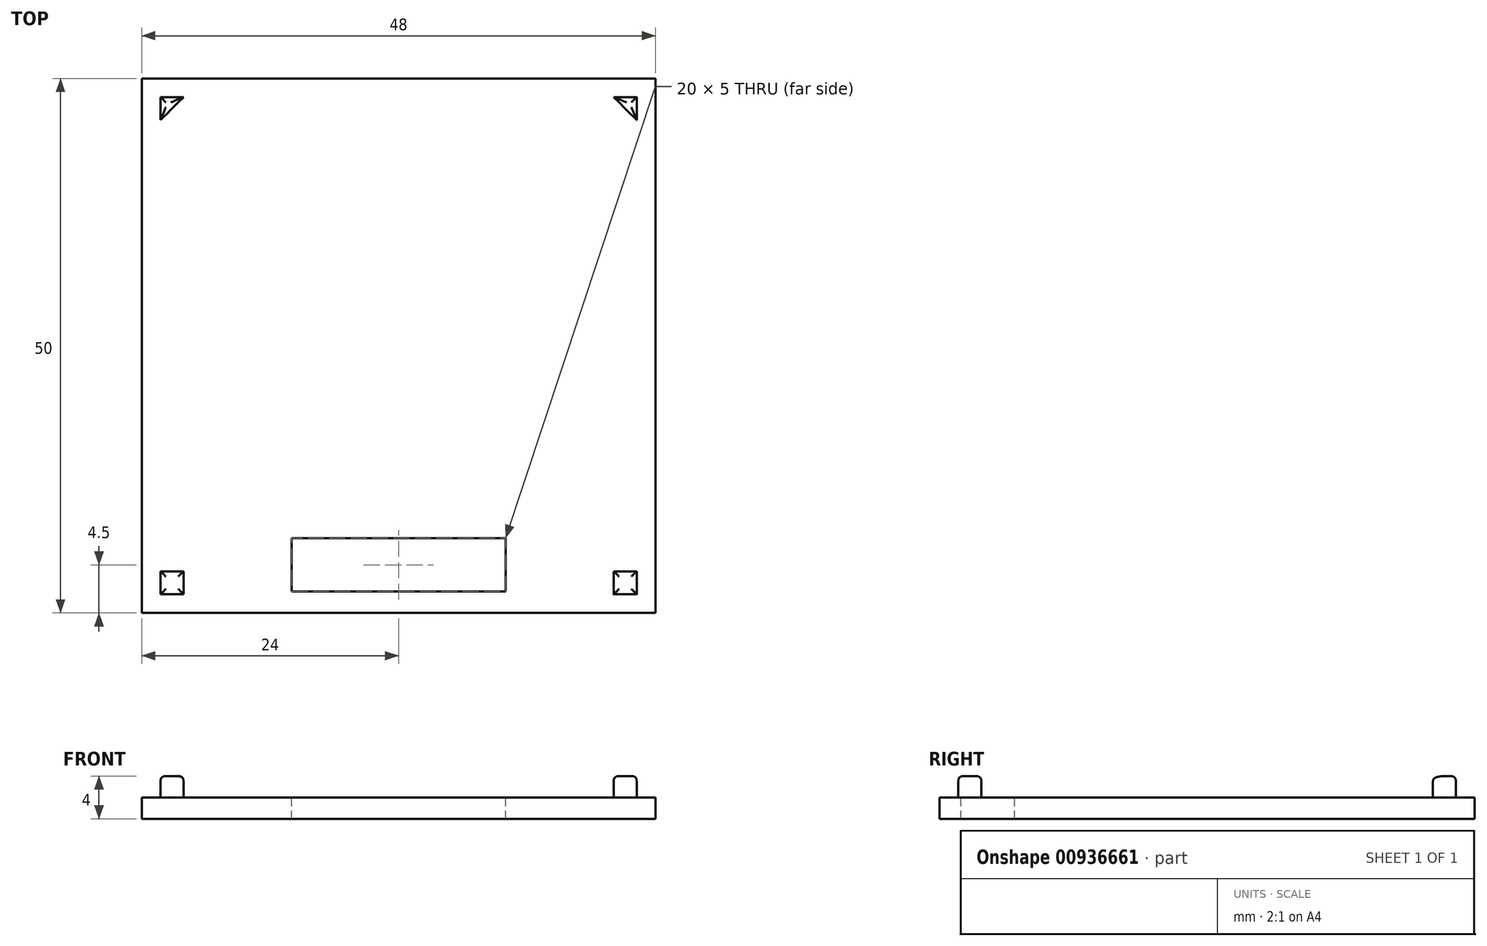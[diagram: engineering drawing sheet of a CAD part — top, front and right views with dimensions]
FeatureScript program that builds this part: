
annotation { "Feature Type Name" : "Feature", "Feature Type Description" : "" }
export const myFeature = defineFeature(function(context is Context, id is Id, definition is map)
    precondition{}
    {
        {
            var Q0;
            Q0=qCreatedBy(makeId("Top.planeOp"),FACE);
            var sketch = newSketch(context, id + "F0", { "sketchPlane" : qUnion([Q0])});
            skLineSegment(sketch, "E0.bottom", {"start": v(0, 0) * mm, "end": v(48, 0) * mm});
            skLineSegment(sketch, "E0.top", {"start": v(0, -50) * mm, "end": v(48, -50) * mm});
            skLineSegment(sketch, "E0.left", {"start": v(0, 0) * mm, "end": v(0, -50) * mm});
            skLineSegment(sketch, "E0.right", {"start": v(48, 0) * mm, "end": v(48, -50) * mm});
            skSolve(sketch);
        }
        {
            var Q0;
            Q0=makeQuery(id+"F0.imprint","IMPRINT",FACE,{"disambiguationData":[TD([[makeQuery(id+"F0.imprint","IMPRINT",EDGE,{"derivedFrom":sQuery(id+"F0.wireOp",EDGE,"8EBudFLo-aEb5-milo-hGKJ-UnPFVyJPno7u")}),1.0]])]});
            var Q1;
            Q1=makeQuery(id+"F0.imprint","IMPRINT",FACE,{"disambiguationData":[TD([[makeQuery(id+"F0.imprint","IMPRINT",EDGE,{"derivedFrom":sQuery(id+"F0.wireOp",EDGE,"b2cc03f5-71c5-4ed7-81ff-36fc711708750.MirrorCS")}),-1.0]])]});
            var Q2;
            Q2=makeQuery(id+"F0.imprint","IMPRINT",FACE,{"disambiguationData":[TD([[makeQuery(id+"F0.imprint","IMPRINT",EDGE,{"derivedFrom":sQuery(id+"F0.wireOp",EDGE,"E0.bottom")}),-1.0]])]});
            extrude(context, id + "F1", {"entities" : qUnion([Q0, Q1, Q2]), "depth" : 2 * mm, "offsetDistance" : 25 * mm});
        }
        {
            var Q0;
            Q0=makeQuery(id+"F1.opExtrude","CAP_FACE",FACE,{"disambiguationData":[OSD([sQuery(id+"F0.wireOp",EDGE,"E0.bottom"),sQuery(id+"F0.wireOp",EDGE,"E0.top"),sQuery(id+"F0.wireOp",EDGE,"E0.left"),sQuery(id+"F0.wireOp",EDGE,"E0.right")])],"isStart":false});
            var sketch = newSketch(context, id + "F2", { "sketchPlane" : qUnion([Q0])});
            skLineSegment(sketch, "E1", {"start": v(1.5, -1.5) * mm, "end": v(1.5, -4.5) * mm, "construction": true});
            skLineSegment(sketch, "E2", {"start": v(1.5, -4.5) * mm, "end": v(4.5, -1.5) * mm, "construction": true});
            skLineSegment(sketch, "E3", {"start": v(4.5, -1.5) * mm, "end": v(1.5, -1.5) * mm, "construction": true});
            skLineSegment(sketch, "E4.0", {"start": v(1.75, -3.9) * mm, "end": v(3.9, -1.75) * mm});
            skLineSegment(sketch, "E4.1", {"start": v(1.75, -1.75) * mm, "end": v(1.75, -3.9) * mm});
            skLineSegment(sketch, "E4.2", {"start": v(3.9, -1.75) * mm, "end": v(1.75, -1.75) * mm});
            skLineSegment(sketch, "E5.0", {"start": v(-5, 5) * mm, "end": v(-5, -55) * mm});
            skLineSegment(sketch, "E5.1", {"start": v(53, 5) * mm, "end": v(-5, 5) * mm});
            skLineSegment(sketch, "E5.2", {"start": v(53, -55) * mm, "end": v(53, 5) * mm});
            skLineSegment(sketch, "E5.3", {"start": v(-5, -55) * mm, "end": v(53, -55) * mm});
            skLineSegment(sketch, "E6", {"start": v(24, 0) * mm, "end": v(24, -10.54) * mm, "construction": true});
            skLineSegment(sketch, "E7", {"start": v(0, -25) * mm, "end": v(10.69, -25) * mm, "construction": true});
            skLineSegment(sketch, "E8.MirrorCS", {"start": v(46.25, -3.9) * mm, "end": v(44.1, -1.75) * mm});
            skLineSegment(sketch, "E9.MirrorCS", {"start": v(46.25, -1.75) * mm, "end": v(46.25, -3.9) * mm});
            skLineSegment(sketch, "E10.MirrorCS", {"start": v(44.1, -1.75) * mm, "end": v(46.25, -1.75) * mm});
            skLineSegment(sketch, "E11.MirrorCS", {"start": v(1.75, -46.1) * mm, "end": v(3.9, -48.25) * mm});
            skLineSegment(sketch, "E12.MirrorCS", {"start": v(3.9, -48.25) * mm, "end": v(1.75, -48.25) * mm});
            skLineSegment(sketch, "E13.MirrorCS", {"start": v(1.75, -48.25) * mm, "end": v(1.75, -46.1) * mm});
            skLineSegment(sketch, "E14.MirrorCS", {"start": v(46.25, -46.1) * mm, "end": v(44.1, -48.25) * mm});
            skLineSegment(sketch, "E15.MirrorCS", {"start": v(46.25, -48.25) * mm, "end": v(46.25, -46.1) * mm});
            skLineSegment(sketch, "E16.MirrorCS", {"start": v(44.1, -48.25) * mm, "end": v(46.25, -48.25) * mm});
            skLineSegment(sketch, "E17", {"start": v(1.75, -46.1) * mm, "end": v(3.9, -46.1) * mm});
            skLineSegment(sketch, "E18", {"start": v(3.9, -46.1) * mm, "end": v(3.9, -48.25) * mm});
            skLineSegment(sketch, "E19", {"start": v(46.25, -46.1) * mm, "end": v(44.1, -46.1) * mm});
            skLineSegment(sketch, "E20", {"start": v(44.1, -46.1) * mm, "end": v(44.1, -48.25) * mm});
            skSolve(sketch);
        }
        {
            var Q0;
            Q0=makeQuery(id+"F2.imprint","IMPRINT",FACE,{"disambiguationData":[TD([[makeQuery(id+"F2.imprint","IMPRINT",EDGE,{"derivedFrom":sQuery(id+"F2.wireOp",EDGE,"E4.0")}),1.0]])]});
            var Q1;
            Q1=makeQuery(id+"F2.imprint","IMPRINT",FACE,{"disambiguationData":[TD([[makeQuery(id+"F2.imprint","IMPRINT",EDGE,{"derivedFrom":sQuery(id+"F2.wireOp",EDGE,"E8.MirrorCS")}),-1.0]])]});
            var Q2;
            Q2=makeQuery(id+"F2.imprint","IMPRINT",FACE,{"disambiguationData":[TD([[makeQuery(id+"F2.imprint","IMPRINT",EDGE,{"derivedFrom":sQuery(id+"F2.wireOp",EDGE,"E14.MirrorCS")}),1.0]])]});
            var Q3;
            Q3=makeQuery(id+"F2.imprint","IMPRINT",FACE,{"disambiguationData":[TD([[makeQuery(id+"F2.imprint","IMPRINT",EDGE,{"derivedFrom":sQuery(id+"F2.wireOp",EDGE,"E11.MirrorCS")}),-1.0]])]});
            var Q4;
            Q4=makeQuery(id+"F2.imprint","IMPRINT",FACE,{"disambiguationData":[TD([[makeQuery(id+"F2.imprint","IMPRINT",EDGE,{"derivedFrom":sQuery(id+"F2.wireOp",EDGE,"E11.MirrorCS")}),1.0]])]});
            var Q5;
            Q5=makeQuery(id+"F2.imprint","IMPRINT",FACE,{"disambiguationData":[TD([[makeQuery(id+"F2.imprint","IMPRINT",EDGE,{"derivedFrom":sQuery(id+"F2.wireOp",EDGE,"E14.MirrorCS")}),-1.0]])]});
            extrude(context, id + "F3", {"entities" : qUnion([Q0, Q1, Q2, Q3, Q4, Q5]), "operationType" : NewBodyOperationType.ADD, "depth" : 2 * mm, "offsetDistance" : 25 * mm});
        }
        {
            var Q0;
            Q0=makeQuery(id+"F1.opExtrude","CAP_FACE",FACE,{"disambiguationData":[OSD([sQuery(id+"F0.wireOp",EDGE,"E0.bottom"),sQuery(id+"F0.wireOp",EDGE,"E0.top"),sQuery(id+"F0.wireOp",EDGE,"E0.left"),sQuery(id+"F0.wireOp",EDGE,"E0.right")])],"isStart":false});
            var sketch = newSketch(context, id + "F4", { "sketchPlane" : qUnion([Q0])});
            skLineSegment(sketch, "E21.bottom", {"start": v(14, -43) * mm, "end": v(34, -43) * mm});
            skLineSegment(sketch, "E21.top", {"start": v(14, -48) * mm, "end": v(34, -48) * mm});
            skLineSegment(sketch, "E21.left", {"start": v(14, -43) * mm, "end": v(14, -48) * mm});
            skLineSegment(sketch, "E21.right", {"start": v(34, -43) * mm, "end": v(34, -48) * mm});
            skLineSegment(sketch, "E22", {"start": v(24, -50) * mm, "end": v(24, -24.04) * mm, "construction": true});
            skPoint(sketch, "E23", {"position": v(24, -48) * mm});
            skSolve(sketch);
        }
        {
            var Q0;
            Q0=makeQuery(id+"F4.imprint","IMPRINT",FACE,{"disambiguationData":[TD([[makeQuery(id+"F4.imprint","IMPRINT",EDGE,{"derivedFrom":sQuery(id+"F4.wireOp",EDGE,"E21.bottom")}),-1.0]])]});
            extrude(context, id + "F5", {"entities" : qUnion([Q0]), "operationType" : NewBodyOperationType.REMOVE, "oppositeDirection" : true, "depth" : 25 * mm, "offsetDistance" : 25 * mm});
        }
        {
            var Q0;
            Q0=makeQuery(id+"F3.opExtrude","CAP_FACE",FACE,{"disambiguationData":[OSD([sQuery(id+"F2.wireOp",EDGE,"E12.MirrorCS"),sQuery(id+"F2.wireOp",EDGE,"E13.MirrorCS"),sQuery(id+"F2.wireOp",EDGE,"E17"),sQuery(id+"F2.wireOp",EDGE,"E18")])],"isStart":false});
            var Q1;
            Q1=makeQuery(id+"F3.opExtrude","CAP_FACE",FACE,{"disambiguationData":[OSD([sQuery(id+"F2.wireOp",EDGE,"E4.0"),sQuery(id+"F2.wireOp",EDGE,"E4.1"),sQuery(id+"F2.wireOp",EDGE,"E4.2")])],"isStart":false});
            var Q2;
            Q2=makeQuery(id+"F3.opExtrude","CAP_FACE",FACE,{"disambiguationData":[OSD([sQuery(id+"F2.wireOp",EDGE,"E8.MirrorCS"),sQuery(id+"F2.wireOp",EDGE,"E9.MirrorCS"),sQuery(id+"F2.wireOp",EDGE,"E10.MirrorCS")])],"isStart":false});
            var Q3;
            Q3=makeQuery(id+"F3.opExtrude","CAP_FACE",FACE,{"disambiguationData":[OSD([sQuery(id+"F2.wireOp",EDGE,"E15.MirrorCS"),sQuery(id+"F2.wireOp",EDGE,"E16.MirrorCS"),sQuery(id+"F2.wireOp",EDGE,"E19"),sQuery(id+"F2.wireOp",EDGE,"E20")])],"isStart":false});
            fillet(context, id + "F6", {"entities" : qUnion([Q0, Q1, Q2, Q3]), "tangentPropagation" : true, "crossSection" : FilletCrossSection.CONIC, "radius" : 0.5 * mm, "rho" : 0.5, "defaultsChanged" : false, "vertexSettings" : [], "allowEdgeOverflow" : false});
        }
    });
